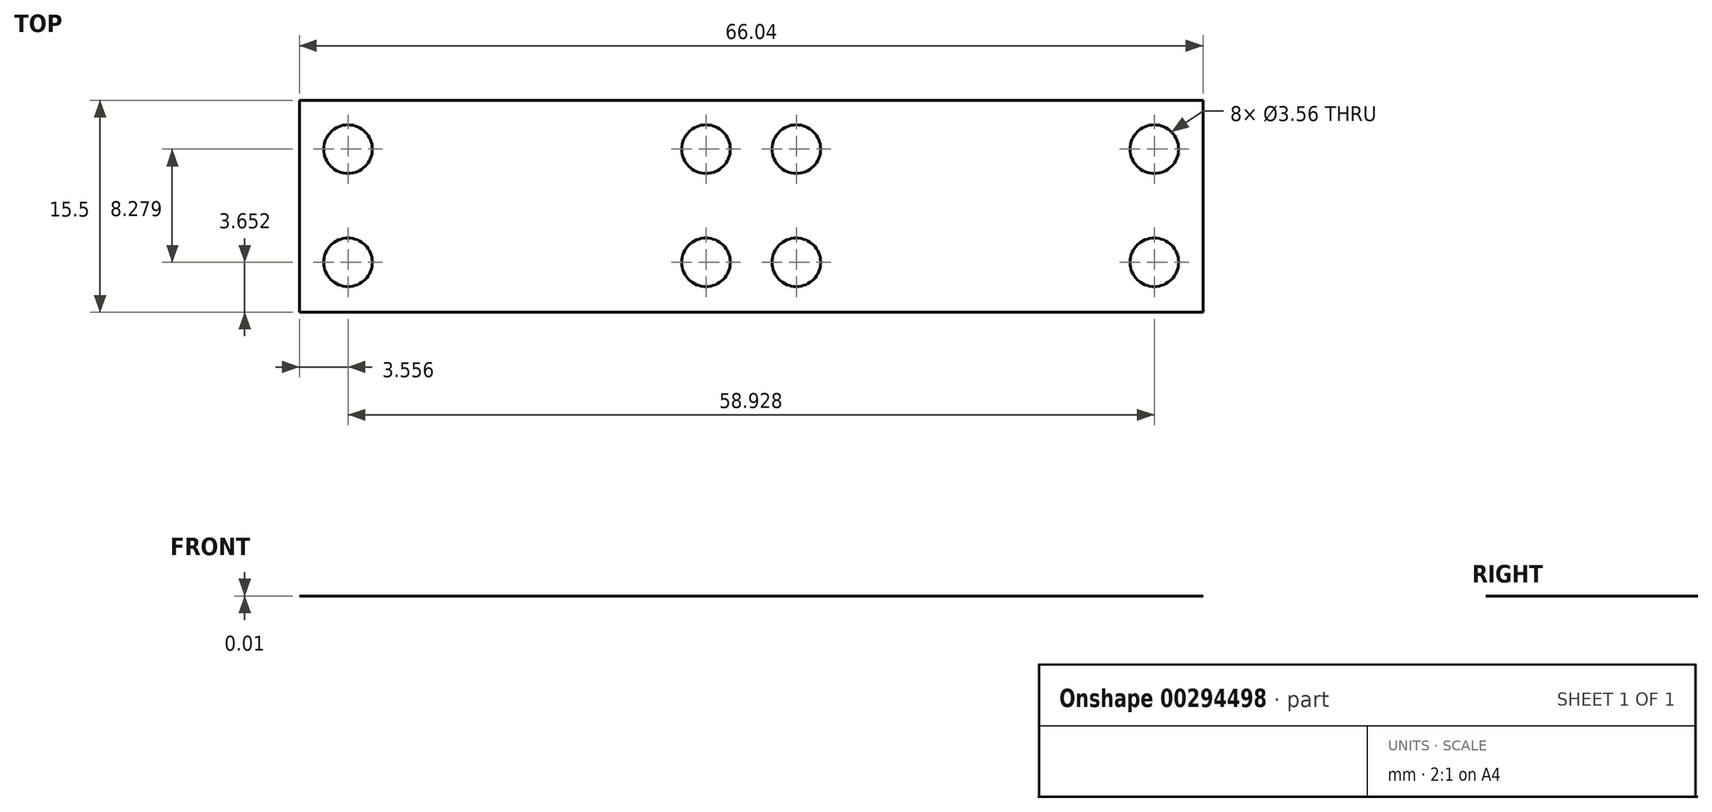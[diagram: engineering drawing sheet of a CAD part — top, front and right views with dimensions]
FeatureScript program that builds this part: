
annotation { "Feature Type Name" : "Feature", "Feature Type Description" : "" }
export const myFeature = defineFeature(function(context is Context, id is Id, definition is map)
    precondition{}
    {
        {
            var Q0;
            Q0=qCreatedBy(makeId("Top.planeOp"),FACE);
            var sketch = newSketch(context, id + "F0", { "sketchPlane" : qUnion([Q0])});
            skLineSegment(sketch, "E0.bottom", {"start": v(33.02, 7.75) * mm, "end": v(-33.02, 7.75) * mm});
            skLineSegment(sketch, "E0.top", {"start": v(33.02, -7.75) * mm, "end": v(-33.02, -7.75) * mm});
            skLineSegment(sketch, "E0.left", {"start": v(33.02, 7.75) * mm, "end": v(33.02, -7.75) * mm});
            skLineSegment(sketch, "E0.right", {"start": v(-33.02, 7.75) * mm, "end": v(-33.02, -7.75) * mm});
            skPoint(sketch, "E0.middle", {"position": v(0, 0) * mm});
            skLineSegment(sketch, "E1", {"start": v(-3.3, 7.75) * mm, "end": v(-3.3, -7.75) * mm});
            skLineSegment(sketch, "E2", {"start": v(3.3, 7.75) * mm, "end": v(3.3, -7.75) * mm});
            skCircle(sketch, "E3", {"center": v(3.3, -4.1) * mm, "radius": 1.78 * mm});
            skCircle(sketch, "E4", {"center": v(3.3, 4.18) * mm, "radius": 1.78 * mm});
            skCircle(sketch, "E5", {"center": v(-3.3, 4.18) * mm, "radius": 1.78 * mm});
            skCircle(sketch, "E6", {"center": v(-3.3, -4.1) * mm, "radius": 1.78 * mm});
            skLineSegment(sketch, "E7", {"start": v(29.46, 7.75) * mm, "end": v(29.46, -7.75) * mm});
            skLineSegment(sketch, "E8", {"start": v(-29.46, 7.75) * mm, "end": v(-29.46, -7.75) * mm});
            skCircle(sketch, "E9", {"center": v(29.46, 4.18) * mm, "radius": 1.78 * mm});
            skCircle(sketch, "E10", {"center": v(29.46, -4.1) * mm, "radius": 1.78 * mm});
            skCircle(sketch, "E11", {"center": v(-29.46, -4.1) * mm, "radius": 1.78 * mm});
            skCircle(sketch, "E12", {"center": v(-29.46, 4.18) * mm, "radius": 1.78 * mm});
            skSolve(sketch);
        }
        {
            var Q0;
            {var subQ1=sQuery(id+"F0.wireOp",EDGE,"E0.bottom");var subQ5=sQuery(id+"F0.wireOp",EDGE,"E1");var subQ6=makeQuery(id+"F0.imprint","INTERSECT",VERTEX,{"derivedFrom":[subQ1,subQ5]});Q0=makeQuery(id+"F0.imprint","IMPRINT",FACE,{"disambiguationData":[TD([[makeQuery(id+"F0.imprint","IMPRINT",EDGE,{"disambiguationData":[TD([[subQ6,-1.0]])],"derivedFrom":subQ1}),1.0]])]});}
            var Q1;
            {var subQ6=sQuery(id+"F0.wireOp",EDGE,"E0.right");Q1=makeQuery(id+"F0.imprint","IMPRINT",FACE,{"disambiguationData":[TD([[makeQuery(id+"F0.imprint","IMPRINT",EDGE,{"derivedFrom":subQ6}),1.0]])]});}
            var Q2;
            {var subQ1=sQuery(id+"F0.wireOp",EDGE,"E2");var subQ16=sQuery(id+"F0.wireOp",EDGE,"E0.bottom");var subQ17=makeQuery(id+"F0.imprint","INTERSECT",VERTEX,{"derivedFrom":[subQ16,subQ1]});Q2=makeQuery(id+"F0.imprint","IMPRINT",FACE,{"disambiguationData":[TD([[makeQuery(id+"F0.imprint","IMPRINT",EDGE,{"disambiguationData":[TD([[subQ17,1.0]])],"derivedFrom":subQ16}),1.0]])]});}
            var Q3;
            {var subQ6=sQuery(id+"F0.wireOp",EDGE,"E0.left");Q3=makeQuery(id+"F0.imprint","IMPRINT",FACE,{"disambiguationData":[TD([[makeQuery(id+"F0.imprint","IMPRINT",EDGE,{"derivedFrom":subQ6}),-1.0]])]});}
            var Q4;
            {var subQ8=sQuery(id+"F0.wireOp",EDGE,"E0.bottom");var subQ11=sQuery(id+"F0.wireOp",EDGE,"E1");var subQ15=makeQuery(id+"F0.imprint","INTERSECT",VERTEX,{"derivedFrom":[subQ8,subQ11]});Q4=makeQuery(id+"F0.imprint","IMPRINT",FACE,{"disambiguationData":[TD([[makeQuery(id+"F0.imprint","IMPRINT",EDGE,{"disambiguationData":[TD([[subQ15,1.0]])],"derivedFrom":subQ8}),1.0]])]});}
            extrude(context, id + "F1", {"entities" : qUnion([Q0, Q1, Q2, Q3, Q4]), "depth" : 3 / 406.4 * mm});
        }
    });
